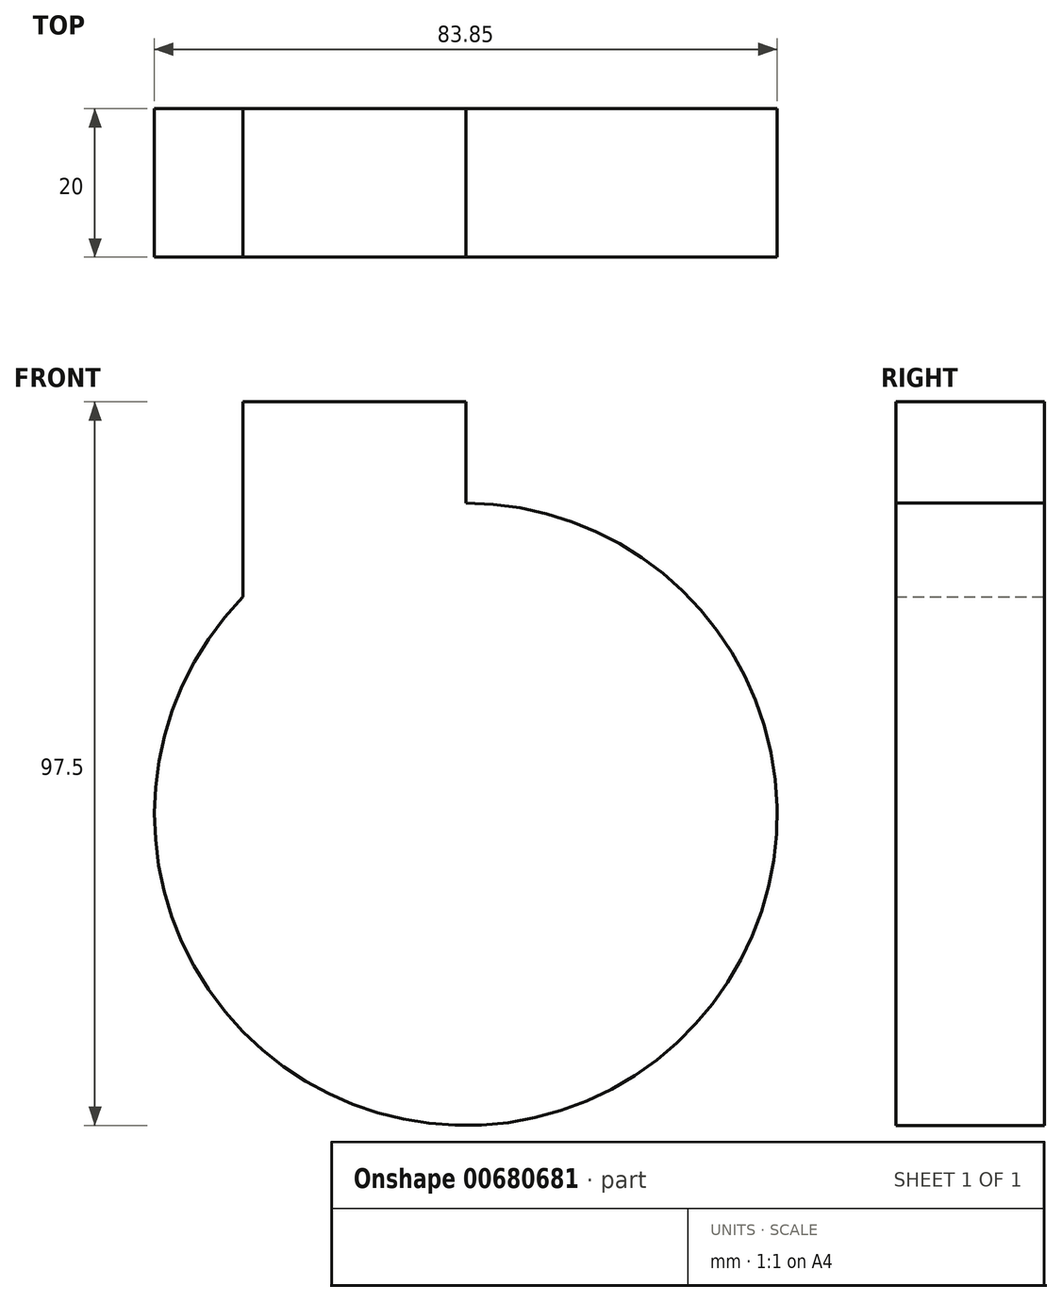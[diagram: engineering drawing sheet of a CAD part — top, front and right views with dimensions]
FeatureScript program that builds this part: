
annotation { "Feature Type Name" : "Feature", "Feature Type Description" : "" }
export const myFeature = defineFeature(function(context is Context, id is Id, definition is map)
    precondition{}
    {
        {
            var Q0;
            Q0=qCreatedBy(makeId("Front.planeOp"),FACE);
            var sketch = newSketch(context, id + "F0", { "sketchPlane" : qUnion([Q0])});
            skCircle(sketch, "E0", {"center": v(0, 0) * mm, "radius": 41.92 * mm});
            skLineSegment(sketch, "E1.bottom", {"start": v(0, 0) * mm, "end": v(-30, 0) * mm});
            skLineSegment(sketch, "E1.top", {"start": v(0, 55.58) * mm, "end": v(-30, 55.58) * mm});
            skLineSegment(sketch, "E1.left", {"start": v(0, 0) * mm, "end": v(0, 55.58) * mm});
            skLineSegment(sketch, "E1.right", {"start": v(-30, 0) * mm, "end": v(-30, 55.58) * mm});
            skSolve(sketch);
        }
        {
            var Q0;
            {var subQ5=sQuery(id+"F0.wireOp",EDGE,"E1.bottom");Q0=makeQuery(id+"F0.imprint","IMPRINT",FACE,{"disambiguationData":[TD([[makeQuery(id+"F0.imprint","IMPRINT",EDGE,{"derivedFrom":subQ5}),1.0]])]});}
            var Q1;
            {var subQ5=sQuery(id+"F0.wireOp",EDGE,"E1.bottom");Q1=makeQuery(id+"F0.imprint","IMPRINT",FACE,{"disambiguationData":[TD([[makeQuery(id+"F0.imprint","IMPRINT",EDGE,{"derivedFrom":subQ5}),-1.0]])]});}
            var Q2;
            {var subQ5=sQuery(id+"F0.wireOp",EDGE,"E1.top");Q2=makeQuery(id+"F0.imprint","IMPRINT",FACE,{"disambiguationData":[TD([[makeQuery(id+"F0.imprint","IMPRINT",EDGE,{"derivedFrom":subQ5}),1.0]])]});}
            extrude(context, id + "F1", {"entities" : qUnion([Q0, Q1, Q2]), "depth" : 20 * mm, "offsetDistance" : 25 * mm});
        }
    });
